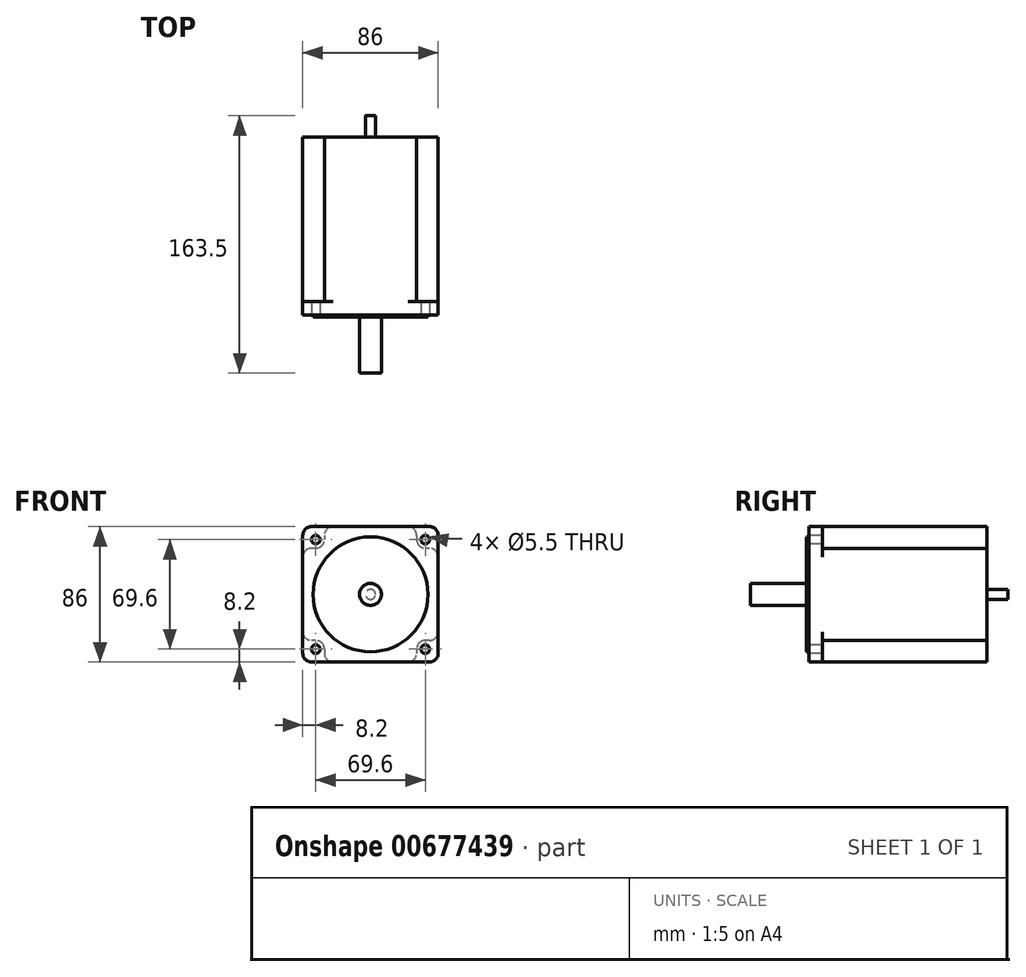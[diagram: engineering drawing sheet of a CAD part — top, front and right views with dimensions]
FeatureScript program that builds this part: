
annotation { "Feature Type Name" : "Feature", "Feature Type Description" : "" }
export const myFeature = defineFeature(function(context is Context, id is Id, definition is map)
    precondition{}
    {
        {
            assignVariable(context, id + "F0", {"name" : "FR", "anyValue" : 5.5});
        }
        {
            var Q0;
            Q0=qCreatedBy(makeId("Front.planeOp"),FACE);
            var sketch = newSketch(context, id + "F1", { "sketchPlane" : qUnion([Q0])});
            skLineSegment(sketch, "E0.bottom", {"start": v(43, 43) * mm, "end": v(-43, 43) * mm});
            skLineSegment(sketch, "E0.top", {"start": v(43, -43) * mm, "end": v(-43, -43) * mm});
            skLineSegment(sketch, "E0.left", {"start": v(43, 43) * mm, "end": v(43, -43) * mm});
            skLineSegment(sketch, "E0.right", {"start": v(-43, 43) * mm, "end": v(-43, -43) * mm});
            skPoint(sketch, "E0.middle", {"position": v(0, 0) * mm});
            skLineSegment(sketch, "E1.bottom", {"start": v(34.8, 34.8) * mm, "end": v(-34.8, 34.8) * mm, "construction": true});
            skLineSegment(sketch, "E1.top", {"start": v(34.8, -34.8) * mm, "end": v(-34.8, -34.8) * mm, "construction": true});
            skLineSegment(sketch, "E1.left", {"start": v(34.8, 34.8) * mm, "end": v(34.8, -34.8) * mm, "construction": true});
            skLineSegment(sketch, "E1.right", {"start": v(-34.8, 34.8) * mm, "end": v(-34.8, -34.8) * mm, "construction": true});
            skCircle(sketch, "E2", {"center": v(34.8, 34.8) * mm, "radius": 2.75 * mm});
            skCircle(sketch, "E3", {"center": v(34.8, -34.8) * mm, "radius": 2.75 * mm});
            skCircle(sketch, "E4", {"center": v(-34.8, -34.8) * mm, "radius": 2.75 * mm});
            skCircle(sketch, "E5", {"center": v(-34.8, 34.8) * mm, "radius": 2.75 * mm});
            skSolve(sketch);
        }
        {
            var Q0;
            Q0 = qSketchRegion(id + "F1", true);
            extrude(context, id + "F2", {"entities" : qUnion([Q0]), "oppositeDirection" : true, "depth" : 8.5 * mm, "offsetDistance" : 25 * mm});
        }
        {
            var Q0;
            Q0=qCreatedBy(makeId("Front.planeOp"),FACE);
            var sketch = newSketch(context, id + "F3", { "sketchPlane" : qUnion([Q0])});
            skCircle(sketch, "E6", {"center": v(0, 0) * mm, "radius": 36.5 * mm});
            skSolve(sketch);
        }
        {
            var Q0;
            Q0 = qSketchRegion(id + "F3", true);
            extrude(context, id + "F4", {"entities" : qUnion([Q0]), "operationType" : NewBodyOperationType.ADD, "depth" : 1.5 * mm, "offsetDistance" : 25 * mm});
        }
        {
            var Q0;
            Q0=qCreatedBy(makeId("Front.planeOp"),FACE);
            var sketch = newSketch(context, id + "F5", { "sketchPlane" : qUnion([Q0])});
            skCircle(sketch, "E7", {"center": v(0, 0) * mm, "radius": 7 * mm});
            skSolve(sketch);
        }
        {
            var Q0;
            Q0 = qSketchRegion(id + "F5", true);
            extrude(context, id + "F6", {"entities" : qUnion([Q0]), "operationType" : NewBodyOperationType.ADD, "depth" : 37 * mm, "offsetDistance" : 25 * mm});
        }
        {
            var Q0;
            Q0=qCreatedBy(makeId("Front.planeOp"),FACE);
            var sketch = newSketch(context, id + "F7", { "sketchPlane" : qUnion([Q0])});
            skArc(sketch, "E8", {"start": v(29.3, 34.8) * mm, "mid": v(30.91, 30.91) * mm, "end": v(34.8, 29.3) * mm});
            skArc(sketch, "E9", {"start": v(34.8, -29.3) * mm, "mid": v(30.91, -30.91) * mm, "end": v(29.3, -34.8) * mm});
            skArc(sketch, "E10", {"start": v(-29.3, -34.8) * mm, "mid": v(-30.91, -30.91) * mm, "end": v(-34.8, -29.3) * mm});
            skArc(sketch, "E11", {"start": v(-34.8, 29.3) * mm, "mid": v(-30.91, 30.91) * mm, "end": v(-29.3, 34.8) * mm});
            skLineSegment(sketch, "E12.bottom", {"start": v(43, 29.3) * mm, "end": v(34.8, 29.3) * mm});
            skLineSegment(sketch, "E12.top", {"start": v(43, -29.3) * mm, "end": v(34.8, -29.3) * mm});
            skLineSegment(sketch, "E12.left", {"start": v(43, 29.3) * mm, "end": v(43, -29.3) * mm});
            skLineSegment(sketch, "E12.right", {"start": v(-43, 29.3) * mm, "end": v(-43, -29.3) * mm});
            skPoint(sketch, "E12.middle", {"position": v(0, 0) * mm});
            skLineSegment(sketch, "E13.bottom", {"start": v(29.3, 43) * mm, "end": v(-29.3, 43) * mm});
            skLineSegment(sketch, "E13.top", {"start": v(29.3, -43) * mm, "end": v(-29.3, -43) * mm});
            skLineSegment(sketch, "E13.left", {"start": v(29.3, 43) * mm, "end": v(29.3, 34.8) * mm});
            skLineSegment(sketch, "E13.right", {"start": v(-29.3, 43) * mm, "end": v(-29.3, 34.8) * mm});
            skLineSegment(sketch, "E14.trimOffspring", {"start": v(-34.8, -29.3) * mm, "end": v(-43, -29.3) * mm});
            skLineSegment(sketch, "E15.trimOffspring", {"start": v(-29.3, -34.8) * mm, "end": v(-29.3, -43) * mm});
            skLineSegment(sketch, "E16.trimOffspring", {"start": v(-34.8, 29.3) * mm, "end": v(-43, 29.3) * mm});
            skLineSegment(sketch, "E17.trimOffspring", {"start": v(29.3, -34.8) * mm, "end": v(29.3, -43) * mm});
            skSolve(sketch);
        }
        {
            var Q0;
            Q0 = qSketchRegion(id + "F7", true);
            extrude(context, id + "F8", {"entities" : qUnion([Q0]), "operationType" : NewBodyOperationType.ADD, "oppositeDirection" : true, "depth" : 113 * mm, "offsetDistance" : 25 * mm});
        }
        {
            var Q0;
            Q0=makeQuery(id+"F8.opExtrude","SWEPT_EDGE",EDGE,{"disambiguationData":[OSD([sQuery(id+"F7.wireOp",EDGE,"E13.bottom"),sQuery(id+"F7.wireOp",EDGE,"E13.left")])]});
            var Q1;
            Q1=makeQuery(id+"F8.opExtrude","SWEPT_EDGE",EDGE,{"disambiguationData":[OSD([sQuery(id+"F7.wireOp",EDGE,"E12.bottom"),sQuery(id+"F7.wireOp",EDGE,"E12.left")])]});
            var Q2;
            Q2=makeQuery(id+"F2.opExtrude","SWEPT_EDGE",EDGE,{"disambiguationData":[OSD([sQuery(id+"F1.wireOp",EDGE,"E0.bottom"),sQuery(id+"F1.wireOp",EDGE,"E0.left")])]});
            var Q3;
            Q3=makeQuery(id+"F8.opExtrude","SWEPT_EDGE",EDGE,{"disambiguationData":[OSD([sQuery(id+"F7.wireOp",EDGE,"E13.bottom"),sQuery(id+"F7.wireOp",EDGE,"E13.right")])]});
            var Q4;
            Q4=makeQuery(id+"F8.opExtrude","SWEPT_EDGE",EDGE,{"disambiguationData":[OSD([sQuery(id+"F7.wireOp",EDGE,"E12.right"),sQuery(id+"F7.wireOp",EDGE,"E16.trimOffspring")])]});
            var Q5;
            Q5=makeQuery(id+"F2.opExtrude","SWEPT_EDGE",EDGE,{"disambiguationData":[OSD([sQuery(id+"F1.wireOp",EDGE,"E0.bottom"),sQuery(id+"F1.wireOp",EDGE,"E0.right")])]});
            var Q6;
            Q6=makeQuery(id+"F8.opExtrude","SWEPT_EDGE",EDGE,{"disambiguationData":[OSD([sQuery(id+"F7.wireOp",EDGE,"E12.top"),sQuery(id+"F7.wireOp",EDGE,"E12.left")])]});
            var Q7;
            Q7=makeQuery(id+"F8.opExtrude","SWEPT_EDGE",EDGE,{"disambiguationData":[OSD([sQuery(id+"F7.wireOp",EDGE,"E13.top"),sQuery(id+"F7.wireOp",EDGE,"E17.trimOffspring")])]});
            var Q8;
            Q8=makeQuery(id+"F2.opExtrude","SWEPT_EDGE",EDGE,{"disambiguationData":[OSD([sQuery(id+"F1.wireOp",EDGE,"E0.top"),sQuery(id+"F1.wireOp",EDGE,"E0.right")])]});
            var Q9;
            Q9=makeQuery(id+"F8.opExtrude","SWEPT_EDGE",EDGE,{"disambiguationData":[OSD([sQuery(id+"F7.wireOp",EDGE,"E13.top"),sQuery(id+"F7.wireOp",EDGE,"E15.trimOffspring")])]});
            var Q10;
            Q10=makeQuery(id+"F8.opExtrude","SWEPT_EDGE",EDGE,{"disambiguationData":[OSD([sQuery(id+"F7.wireOp",EDGE,"E12.right"),sQuery(id+"F7.wireOp",EDGE,"E14.trimOffspring")])]});
            var Q11;
            Q11=makeQuery(id+"F2.opExtrude","SWEPT_EDGE",EDGE,{"disambiguationData":[OSD([sQuery(id+"F1.wireOp",EDGE,"E0.top"),sQuery(id+"F1.wireOp",EDGE,"E0.left")])]});
            fillet(context, id + "F9", {"entities" : qUnion([Q0, Q1, Q2, Q3, Q4, Q5, Q6, Q7, Q8, Q9, Q10, Q11]), "radius" : getVariable(context, 'FR') * mm, "tangentPropagation" : true, "allowEdgeOverflow" : false});
        }
        {
            var Q0;
            Q0=makeQuery(id+"F8.opExtrude","CAP_FACE",FACE,{"disambiguationData":[OSD([sQuery(id+"F7.wireOp",EDGE,"E8"),sQuery(id+"F7.wireOp",EDGE,"E9"),sQuery(id+"F7.wireOp",EDGE,"E10"),sQuery(id+"F7.wireOp",EDGE,"E11"),sQuery(id+"F7.wireOp",EDGE,"E12.bottom"),sQuery(id+"F7.wireOp",EDGE,"E12.top"),sQuery(id+"F7.wireOp",EDGE,"E12.left"),sQuery(id+"F7.wireOp",EDGE,"E12.right"),sQuery(id+"F7.wireOp",EDGE,"E13.bottom"),sQuery(id+"F7.wireOp",EDGE,"E13.top"),sQuery(id+"F7.wireOp",EDGE,"E13.left"),sQuery(id+"F7.wireOp",EDGE,"E13.right"),sQuery(id+"F7.wireOp",EDGE,"E14.trimOffspring"),sQuery(id+"F7.wireOp",EDGE,"E15.trimOffspring"),sQuery(id+"F7.wireOp",EDGE,"E16.trimOffspring"),sQuery(id+"F7.wireOp",EDGE,"E17.trimOffspring")])],"isStart":false});
            var sketch = newSketch(context, id + "F10", { "sketchPlane" : qUnion([Q0])});
            skCircle(sketch, "E18", {"center": v(0, 0) * mm, "radius": 3.17 * mm});
            skSolve(sketch);
        }
        {
            var Q0;
            Q0 = qSketchRegion(id + "F10", true);
            extrude(context, id + "F11", {"entities" : qUnion([Q0]), "operationType" : NewBodyOperationType.ADD, "depth" : 13.5 * mm, "offsetDistance" : 25 * mm});
        }
    });
